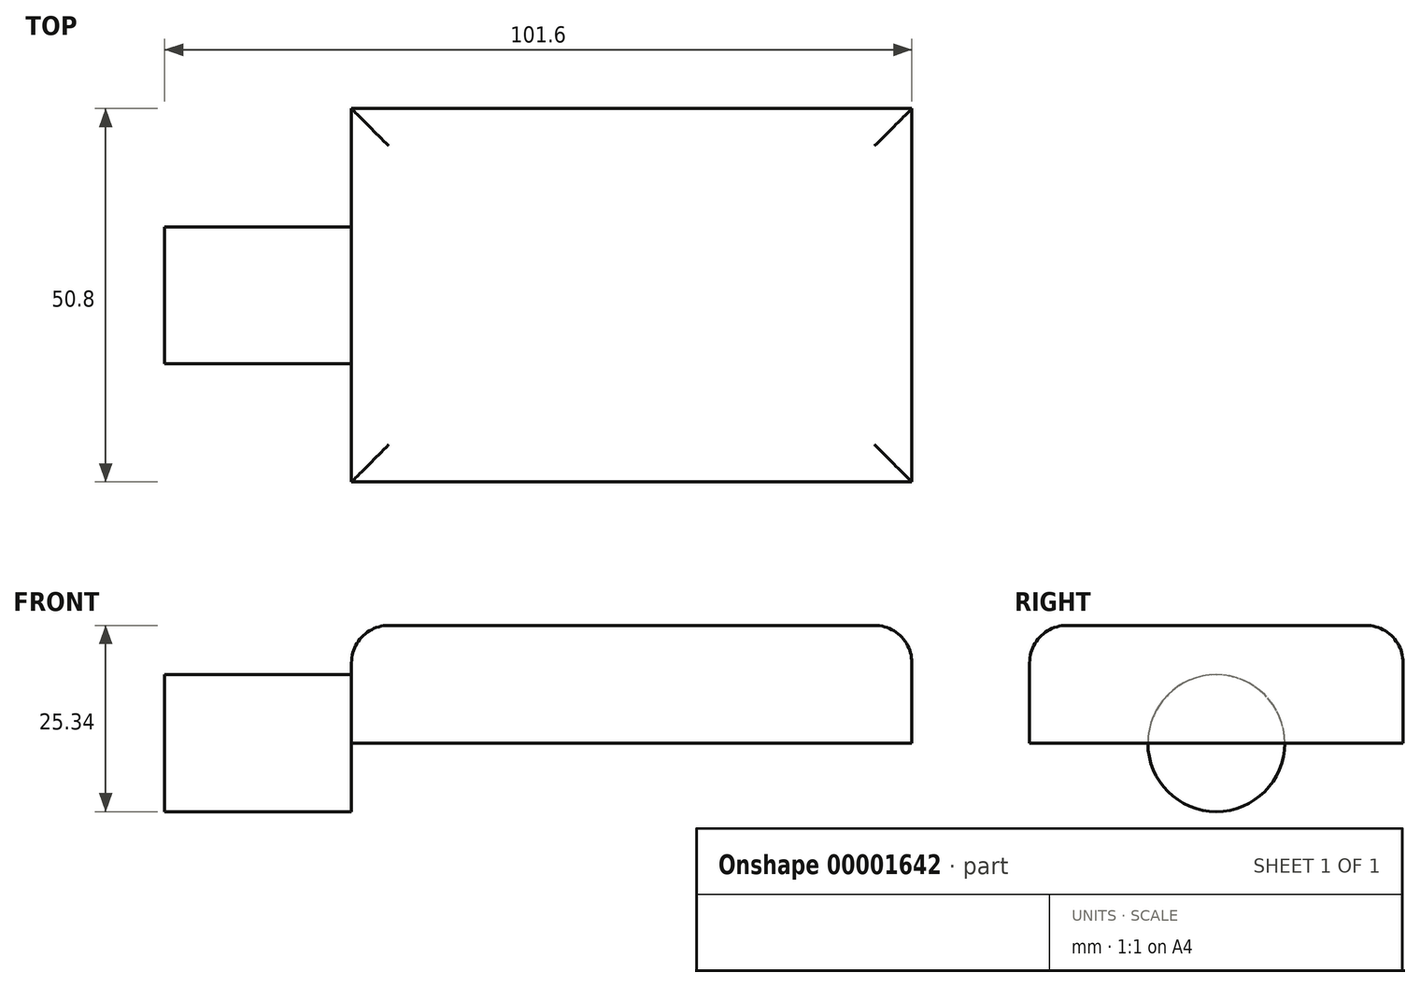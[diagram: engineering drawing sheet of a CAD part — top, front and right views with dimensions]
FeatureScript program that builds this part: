
annotation { "Feature Type Name" : "Feature", "Feature Type Description" : "" }
export const myFeature = defineFeature(function(context is Context, id is Id, definition is map)
    precondition{}
    {
        {
            var Q0;
            Q0=qCreatedBy(makeId("Top.planeOp"),FACE);
            var sketch = newSketch(context, id + "F0", { "sketchPlane" : qUnion([Q0])});
            skLineSegment(sketch, "E0.bottom", {"start": v(-38.1, 25.4) * mm, "end": v(38.1, 25.4) * mm});
            skLineSegment(sketch, "E0.top", {"start": v(-38.1, -25.4) * mm, "end": v(38.1, -25.4) * mm});
            skLineSegment(sketch, "E0.left", {"start": v(-38.1, 25.4) * mm, "end": v(-38.1, -25.4) * mm});
            skLineSegment(sketch, "E0.right", {"start": v(38.1, 25.4) * mm, "end": v(38.1, -25.4) * mm});
            skSolve(sketch);
        }
        {
            var Q0;
            Q0 = qSketchRegion(id + "F0", true);
            extrude(context, id + "F1", {"entities" : qUnion([Q0]), "depth" : 16.03 * mm});
        }
        {
            var Q0;
            Q0=makeQuery(id+"F1.opExtrude","CAP_EDGE",EDGE,{"disambiguationData":[OSD([sQuery(id+"F0.wireOp",EDGE,"E0.left")])],"isStart":false});
            var Q1;
            Q1=makeQuery(id+"F1.opExtrude","CAP_EDGE",EDGE,{"disambiguationData":[OSD([sQuery(id+"F0.wireOp",EDGE,"E0.top")])],"isStart":false});
            var Q2;
            Q2=makeQuery(id+"F1.opExtrude","CAP_EDGE",EDGE,{"disambiguationData":[OSD([sQuery(id+"F0.wireOp",EDGE,"E0.right")])],"isStart":false});
            var Q3;
            Q3=makeQuery(id+"F1.opExtrude","CAP_EDGE",EDGE,{"disambiguationData":[OSD([sQuery(id+"F0.wireOp",EDGE,"E0.bottom")])],"isStart":false});
            fillet(context, id + "F2", {"entities" : qUnion([Q0, Q1, Q2, Q3]), "radius" : 5.08 * mm, "tangentPropagation" : true, "allowEdgeOverflow" : false});
        }
        {
            var Q0;
            Q0=makeQuery(id+"F1.opExtrude","SWEPT_FACE",FACE,{"disambiguationData":[OSD([sQuery(id+"F0.wireOp",EDGE,"E0.left")])]});
            var sketch = newSketch(context, id + "F3", { "sketchPlane" : qUnion([Q0])});
            skCircle(sketch, "E1", {"center": v(0, 0) * mm, "radius": 9.3 * mm});
            skSolve(sketch);
        }
        {
            var Q0;
            Q0 = qSketchRegion(id + "F3", true);
            extrude(context, id + "F4", {"entities" : qUnion([Q0]), "operationType" : NewBodyOperationType.ADD, "depth" : 25.4 * mm});
        }
    });
